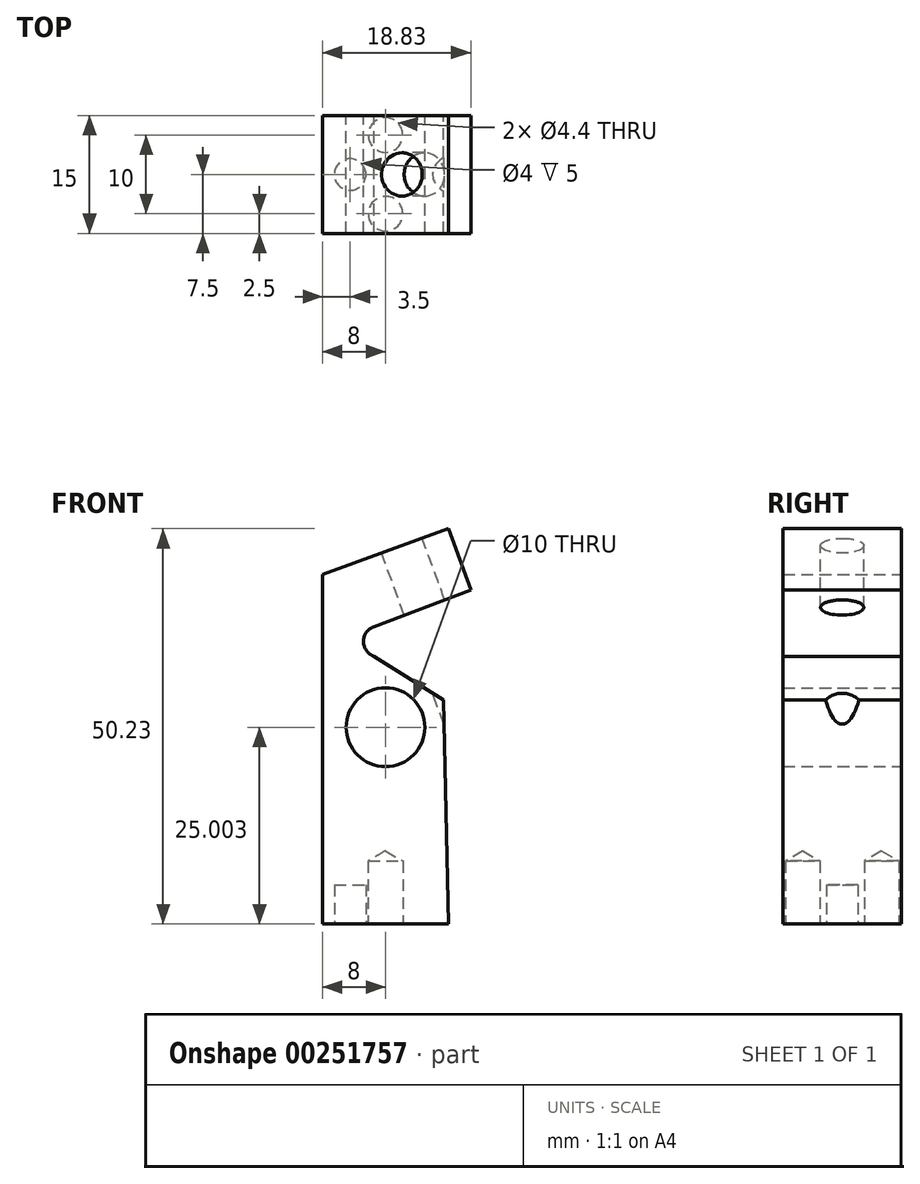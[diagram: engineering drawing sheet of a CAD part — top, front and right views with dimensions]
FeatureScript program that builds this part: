
annotation { "Feature Type Name" : "Feature", "Feature Type Description" : "" }
export const myFeature = defineFeature(function(context is Context, id is Id, definition is map)
    precondition{}
    {
        {
            var Q0;
            Q0=qCreatedBy(makeId("Front.planeOp"),FACE);
            var sketch = newSketch(context, id + "F0", { "sketchPlane" : qUnion([Q0])});
            skLineSegment(sketch, "E0.bottom", {"start": v(8, -18.93) * mm, "end": v(-8, -18.93) * mm});
            skLineSegment(sketch, "E0.left", {"start": v(8, -18.93) * mm, "end": v(7.34, 9.53) * mm});
            skPoint(sketch, "E0.middle", {"position": v(0, 0) * mm});
            skCircle(sketch, "E1", {"center": v(0, 6.07) * mm, "radius": 5 * mm});
            skLineSegment(sketch, "E2", {"start": v(-8, -18.93) * mm, "end": v(-8, 25.47) * mm});
            skLineSegment(sketch, "E3", {"start": v(-1.46, 15.08) * mm, "end": v(7.36, 9.52) * mm});
            skLineSegment(sketch, "E4", {"start": v(-8, 25.47) * mm, "end": v(8, 31.3) * mm});
            skLineSegment(sketch, "E5", {"start": v(8, 31.3) * mm, "end": v(10.83, 23.5) * mm});
            skLineSegment(sketch, "E6", {"start": v(-1.5, 18.84) * mm, "end": v(10.83, 23.5) * mm});
            skPoint(sketch, "E7.center.orphan", {"position": v(-0.8, 16.97) * mm});
            skArc(sketch, "E8", {"start": v(-1.5, 18.84) * mm, "mid": v(-2.8, 16.95) * mm, "end": v(-1.46, 15.08) * mm});
            skSolve(sketch);
        }
        {
            var Q0;
            Q0 = qSketchRegion(id + "F0", true);
            extrude(context, id + "F1", {"entities" : qUnion([Q0]), "depth" : 15 * mm});
        }
        {
            var Q0;
            Q0=makeQuery(id+"F1.opExtrude","SWEPT_FACE",FACE,{"disambiguationData":[OSD([sQuery(id+"F0.wireOp",EDGE,"E4")])]});
            var sketch = newSketch(context, id + "F2", { "sketchPlane" : qUnion([Q0])});
            skPoint(sketch, "E9", {"position": v(11.92, -7.5) * mm});
            skSolve(sketch);
        }
        {
            var Q0;
            Q0=sQuery(id+"F2.wireOp",VERTEX,"E9");
            var Q1;
            Q1=makeQuery(id+"F1.opExtrude","SWEPT_BODY",BODY,{"disambiguationData":[OSD([sQuery(id+"F0.wireOp",EDGE,"E0.bottom"),sQuery(id+"F0.wireOp",EDGE,"E0.left"),sQuery(id+"F0.wireOp",EDGE,"E1"),sQuery(id+"F0.wireOp",EDGE,"E2"),sQuery(id+"F0.wireOp",EDGE,"E3"),sQuery(id+"F0.wireOp",EDGE,"E4"),sQuery(id+"F0.wireOp",EDGE,"E5"),sQuery(id+"F0.wireOp",EDGE,"E6"),sQuery(id+"F0.wireOp",EDGE,"E8")])]});
            hole(context, id + "F3", {"style" : HoleStyle.SIMPLE, "endStyle" : HoleEndStyle.BLIND, "standardTappedOrClearance" : lookupTablePath({ "standard" : "ISO", "fit" : "Normal", "size" : "M5", "type" : "Clearance" }), "standardBlindInLast" : lookupTablePath({ "fit" : "Standard", "standard" : "ISO", "size" : "M5", "type" : "Clearance" }), "holeDiameter" : 5.5 * mm, "holeDepth" : 50 * mm, "isTappedThrough" : true, "tappedDepth" : 12 * mm, "tapClearance" : 3, "locations" : qUnion([Q0]), "scope" : qUnion([Q1])});
        }
        {
            var Q0;
            Q0=makeQuery(id+"F1.opExtrude","SWEPT_FACE",FACE,{"disambiguationData":[OSD([sQuery(id+"F0.wireOp",EDGE,"E0.bottom")])]});
            var sketch = newSketch(context, id + "F4", { "sketchPlane" : qUnion([Q0])});
            skPoint(sketch, "E10", {"position": v(0, 12.5) * mm});
            skPoint(sketch, "E11", {"position": v(0, 2.5) * mm});
            skSolve(sketch);
        }
        {
            var Q0;
            Q0=sQuery(id+"F4.wireOp",VERTEX,"E10");
            var Q1;
            Q1=sQuery(id+"F4.wireOp",VERTEX,"E11");
            var Q2;
            Q2=makeQuery(id+"F1.opExtrude","SWEPT_BODY",BODY,{"disambiguationData":[OSD([sQuery(id+"F0.wireOp",EDGE,"E0.bottom"),sQuery(id+"F0.wireOp",EDGE,"E0.left"),sQuery(id+"F0.wireOp",EDGE,"E1"),sQuery(id+"F0.wireOp",EDGE,"E2"),sQuery(id+"F0.wireOp",EDGE,"E3"),sQuery(id+"F0.wireOp",EDGE,"E4"),sQuery(id+"F0.wireOp",EDGE,"E5"),sQuery(id+"F0.wireOp",EDGE,"E6"),sQuery(id+"F0.wireOp",EDGE,"E8")])]});
            hole(context, id + "F5", {"style" : HoleStyle.SIMPLE, "endStyle" : HoleEndStyle.BLIND, "standardTappedOrClearance" : lookupTablePath({ "standard" : "ISO", "fit" : "Normal", "size" : "M4", "type" : "Clearance" }), "standardBlindInLast" : lookupTablePath({ "fit" : "Standard", "standard" : "ISO", "size" : "M4", "type" : "Clearance" }), "holeDiameter" : 4.4 * mm, "holeDepth" : 8 * mm, "isTappedThrough" : true, "tappedDepth" : 12 * mm, "tapClearance" : 3, "locations" : qUnion([Q0, Q1]), "scope" : qUnion([Q2])});
        }
        {
            var Q0;
            Q0=makeQuery(id+"F1.opExtrude","SWEPT_FACE",FACE,{"disambiguationData":[OSD([sQuery(id+"F0.wireOp",EDGE,"E0.bottom")])]});
            var sketch = newSketch(context, id + "F6", { "sketchPlane" : qUnion([Q0])});
            skCircle(sketch, "E12", {"center": v(-4.5, 7.5) * mm, "radius": 2 * mm});
            skSolve(sketch);
        }
        {
            var Q0;
            Q0 = qSketchRegion(id + "F6", true);
            extrude(context, id + "F7", {"entities" : qUnion([Q0]), "operationType" : NewBodyOperationType.REMOVE, "oppositeDirection" : true, "depth" : 5 * mm});
        }
    });
